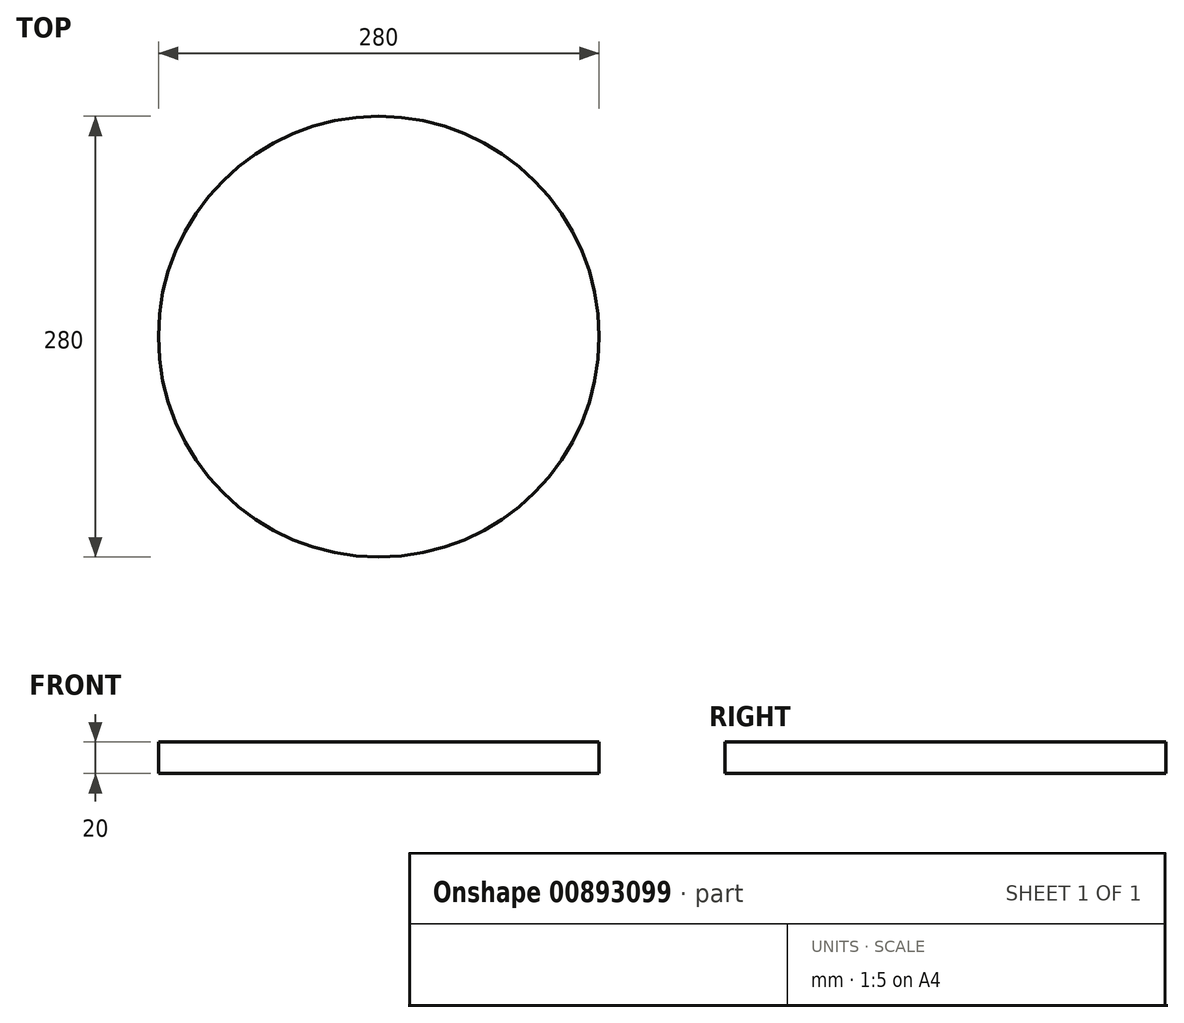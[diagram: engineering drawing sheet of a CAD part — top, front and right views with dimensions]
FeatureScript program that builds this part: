
annotation { "Feature Type Name" : "Feature", "Feature Type Description" : "" }
export const myFeature = defineFeature(function(context is Context, id is Id, definition is map)
    precondition{}
    {
        {
            var Q0;
            Q0=qCreatedBy(makeId("Top.planeOp"),FACE);
            var sketch = newSketch(context, id + "F0", { "sketchPlane" : qUnion([Q0])});
            skCircle(sketch, "E0", {"center": v(0, 0) * mm, "radius": 140 * mm});
            skSolve(sketch);
        }
        {
            var Q0;
            Q0=makeQuery(id+"F0.imprint","IMPRINT",FACE,{"disambiguationData":[TD([[makeQuery(id+"F0.imprint","IMPRINT",EDGE,{"derivedFrom":sQuery(id+"F0.wireOp",EDGE,"E0")}),1.0]])]});
            extrude(context, id + "F1", {"entities" : qUnion([Q0]), "depth" : 20 * mm, "offsetDistance" : 25 * mm});
        }
    });
